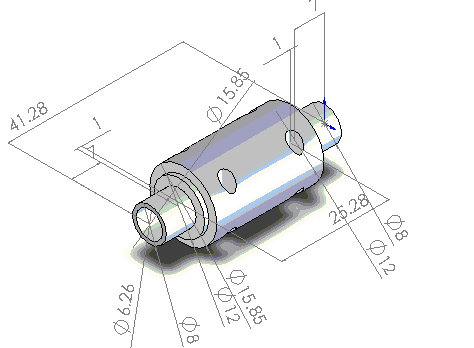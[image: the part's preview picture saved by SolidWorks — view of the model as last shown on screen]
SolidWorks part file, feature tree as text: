
SOLIDWORKS PART (.sldprt)
format: sldprt  version: not decoded by parser v0  size: 314,368 bytes
history: native  units: mm
features: sketch x7, cut_extrude x6, extrude x1 + 1 further entry (+10 scaffold rows collapsed)
feature tree (25):
  "Annotations"  RD1=15.85mm RD2=41.28mm RD3=12mm RD4=15.85mm RD5=25.28mm RD6=7mm RD7=1mm RD8=7mm RD9=1mm RD10=8mm RD11=6.26mm RD12=12mm RD13=8mm
  scaffold x10  (default folders/planes/origin — collapsed)
  sketch  "Sketch1"  dims[D1=~4.59375mm]
  extrude  "Extrude1"  Depth=41.28mm
  sketch  "Sketch2"  dims[D1=~7.807874mm]
  cut_extrude  "Cut-Extrude1"  Depth=7mm
  sketch  "Sketch3"  dims[D1=~1.53125mm]
  cut_extrude  "Cut-Extrude2"  Depth=27mm
  sketch  "Sketch4"  dims[D1=~7.65625mm]
  cut_extrude  "Cut-Extrude3"  Depth=7mm
  sketch  "Sketch5"  dims[D1=~6.313505mm]
  cut_extrude  "Cut-Extrude5"  Depth=1mm
  sketch  "Sketch6"  dims[D1=~4.842238mm]
  cut_extrude  "Cut-Extrude6"  Depth=1mm
  sketch  "Sketch7"  dims[D1=~1.53125mm]
  cut_extrude  "Cut-Extrude7"  [1 undecoded]
decode coverage: 13 of 14 modeling features carry decoded parameters; 1 rows unclassified (native names shown)
note: ~ marks probable driven/reference dimensions
note: 1 parameter value undecoded
note: suppression state not decoded; provenance and decode notes live in map.json
